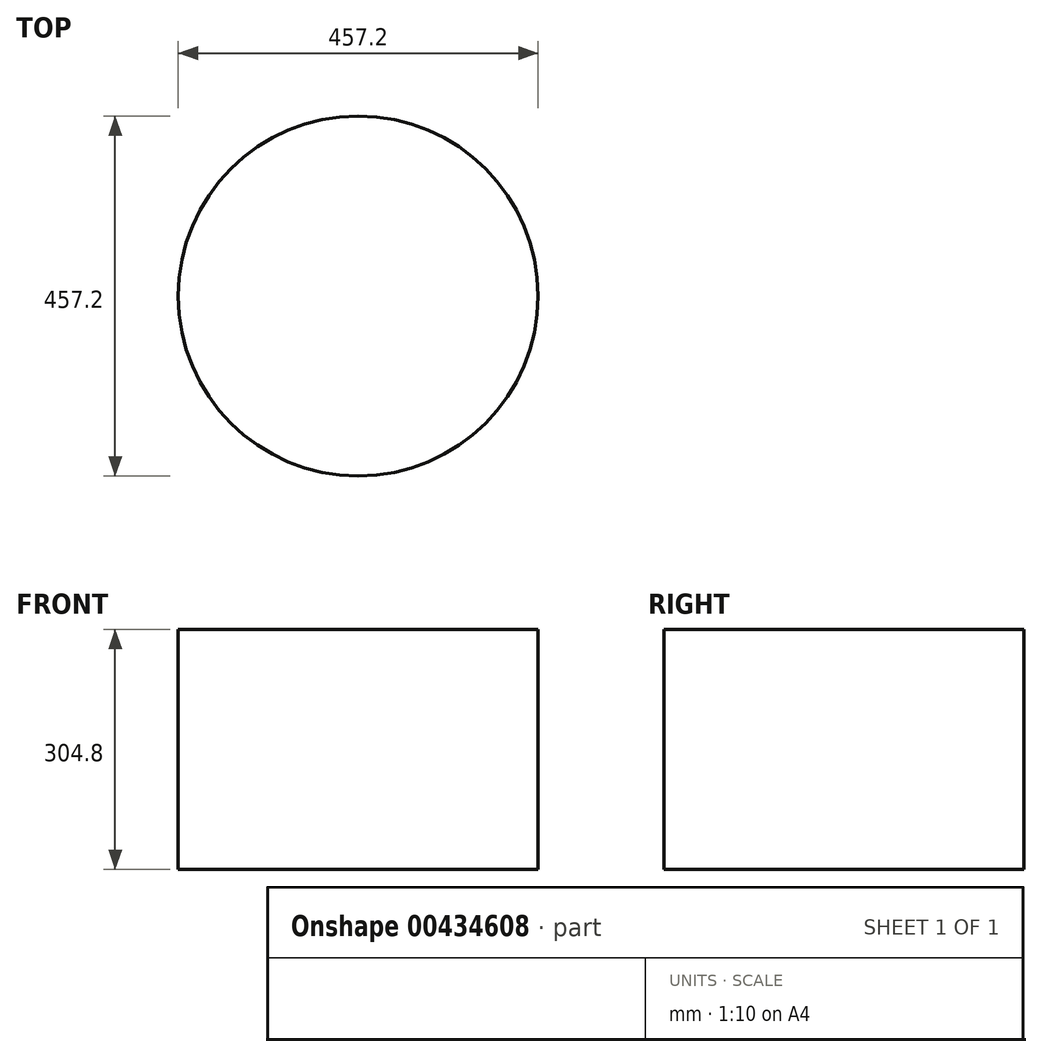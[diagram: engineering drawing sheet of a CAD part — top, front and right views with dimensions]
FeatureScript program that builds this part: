
annotation { "Feature Type Name" : "Feature", "Feature Type Description" : "" }
export const myFeature = defineFeature(function(context is Context, id is Id, definition is map)
    precondition{}
    {
        {
            var Q0;
            Q0=qCreatedBy(makeId("Top.planeOp"),FACE);
            var sketch = newSketch(context, id + "F0", { "sketchPlane" : qUnion([Q0])});
            skCircle(sketch, "E0", {"center": v(0, 0) * mm, "radius": 228.6 * mm});
            skSolve(sketch);
        }
        {
            var Q0;
            Q0=makeQuery(id+"F0.imprint","IMPRINT",FACE,{"disambiguationData":[TD([[makeQuery(id+"F0.imprint","IMPRINT",EDGE,{"derivedFrom":sQuery(id+"F0.wireOp",EDGE,"E0")}),1.0]])]});
            var Q1;
            Q1=sQuery(id+"F0.wireOp",EDGE,"E0");
            extrude(context, id + "F1", {"entities" : qUnion([Q0]), "bodyType" : ToolBodyType.SURFACE, "surfaceEntities" : qUnion([Q1]), "depth" : 304.8 * mm});
        }
    });
